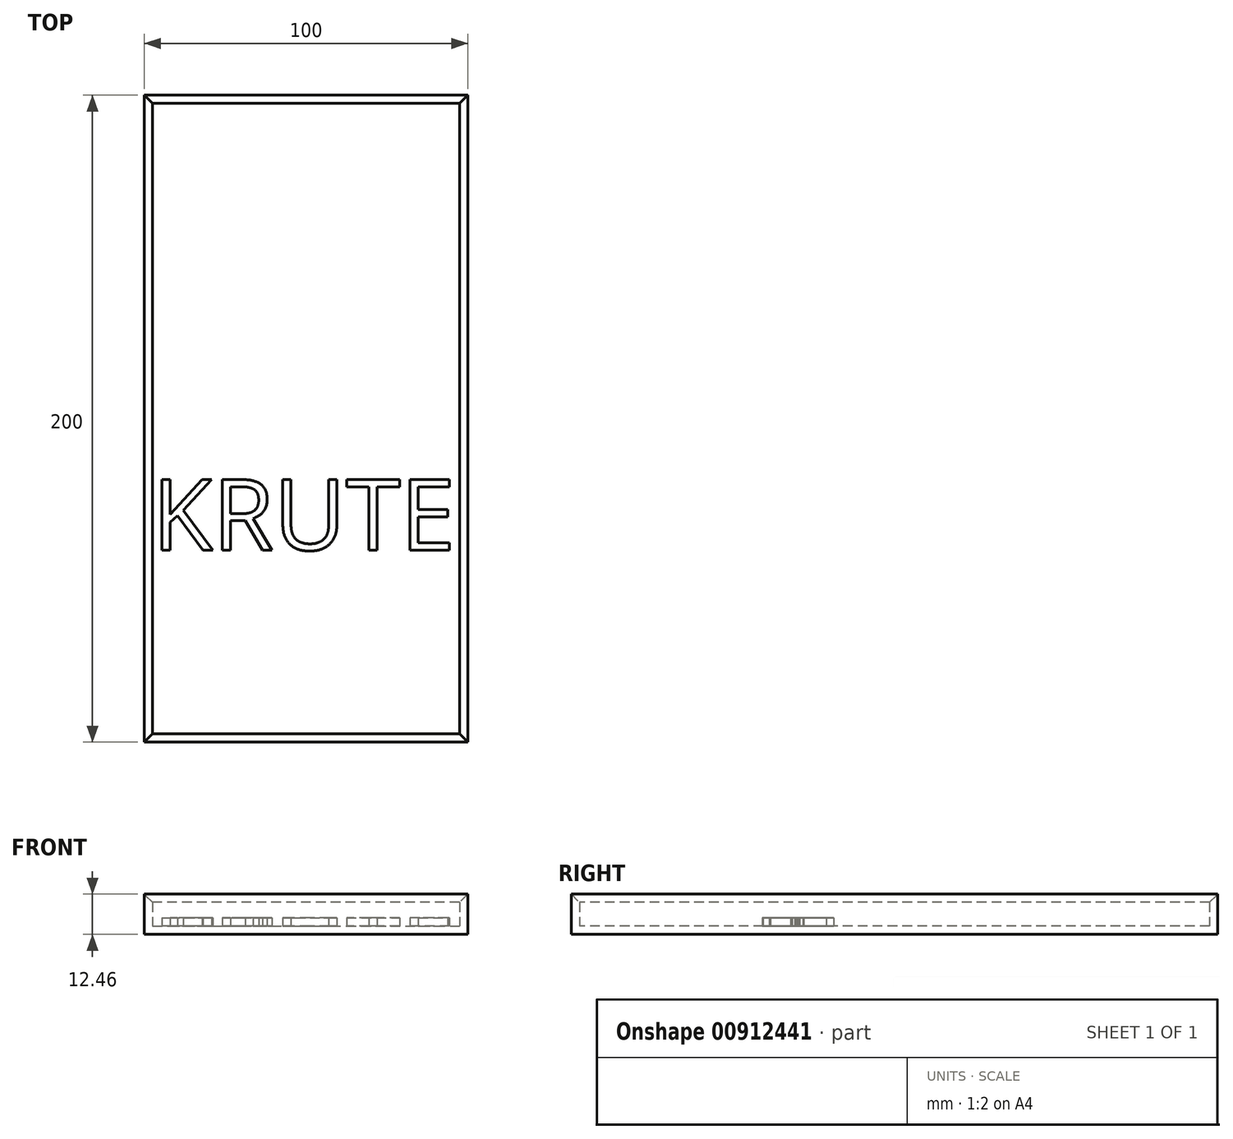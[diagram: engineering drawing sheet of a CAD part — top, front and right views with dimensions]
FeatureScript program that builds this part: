
annotation { "Feature Type Name" : "Feature", "Feature Type Description" : "" }
export const myFeature = defineFeature(function(context is Context, id is Id, definition is map)
    precondition{}
    {
        {
            var Q0;
            Q0=qCreatedBy(makeId("Top.planeOp"),FACE);
            var sketch = newSketch(context, id + "F0", { "sketchPlane" : qUnion([Q0])});
            skLineSegment(sketch, "E0.bottom", {"start": v(-49.36, 118.64) * mm, "end": v(50.64, 118.64) * mm});
            skLineSegment(sketch, "E0.top", {"start": v(-49.36, -81.36) * mm, "end": v(50.64, -81.36) * mm});
            skLineSegment(sketch, "E0.left", {"start": v(-49.36, 118.64) * mm, "end": v(-49.36, -81.36) * mm});
            skLineSegment(sketch, "E0.right", {"start": v(50.64, 118.64) * mm, "end": v(50.64, -81.36) * mm});
            skSolve(sketch);
        }
        {
            var Q0;
            Q0 = qSketchRegion(id + "F0", true);
            extrude(context, id + "F1", {"entities" : qUnion([Q0]), "depth" : 15 * mm, "offsetDistance" : 25.4 * mm});
        }
        {
            var Q0;
            Q0=makeQuery(id+"F1.opExtrude","CAP_FACE",FACE,{"disambiguationData":[OSD([sQuery(id+"F0.wireOp",EDGE,"E0.bottom"),sQuery(id+"F0.wireOp",EDGE,"E0.top"),sQuery(id+"F0.wireOp",EDGE,"E0.left"),sQuery(id+"F0.wireOp",EDGE,"E0.right")])],"isStart":false});
            shell(context, id + "F2", {"entities" : qUnion([Q0]), "thickness" : 2.54 * mm});
        }
        {
            var Q0;
            Q0=makeQuery(id+"F2.opShell","OFFSET_FACE",FACE,{"disambiguationData":[OSD([sQuery(id+"F0.wireOp",EDGE,"E0.bottom"),sQuery(id+"F0.wireOp",EDGE,"E0.top"),sQuery(id+"F0.wireOp",EDGE,"E0.left"),sQuery(id+"F0.wireOp",EDGE,"E0.right")])]});
            var sketch = newSketch(context, id + "F3", { "sketchPlane" : qUnion([Q0])});
            skText(sketch, "E1", { "text": "KRUTE", "fontName": "OpenSans-Regular.ttf"});
            const initialGuessF3  = {"E1": [-0.04694, -0.022, 1, 0, 0.022]};
            skSetInitialGuess(sketch, initialGuessF3);
            skSolve(sketch);
        }
        {
            var Q0;
            Q0 = qSketchRegion(id + "F3", true);
            extrude(context, id + "F4", {"entities" : qUnion([Q0]), "operationType" : NewBodyOperationType.ADD, "depth" : 2.54 * mm, "offsetDistance" : 25.4 * mm});
        }
        {
            var Q0;
            {var subQ0=sQuery(id+"F0.wireOp",EDGE,"E0.left");Q0=makeQuery(id+"F2.opShell","OFFSET_EDGE",EDGE,{"disambiguationData":[OSD([subQ0]),TDD([makeQuery(id+"F1.opExtrude","CAP_EDGE",EDGE,{"disambiguationData":[OSD([subQ0])],"isStart":false})])]});}
            var Q1;
            {var subQ0=sQuery(id+"F0.wireOp",EDGE,"E0.top");Q1=makeQuery(id+"F2.opShell","OFFSET_EDGE",EDGE,{"disambiguationData":[OSD([subQ0]),TDD([makeQuery(id+"F1.opExtrude","CAP_EDGE",EDGE,{"disambiguationData":[OSD([subQ0])],"isStart":false})])]});}
            var Q2;
            {var subQ0=sQuery(id+"F0.wireOp",EDGE,"E0.right");Q2=makeQuery(id+"F2.opShell","OFFSET_EDGE",EDGE,{"disambiguationData":[OSD([subQ0]),TDD([makeQuery(id+"F1.opExtrude","CAP_EDGE",EDGE,{"disambiguationData":[OSD([subQ0])],"isStart":false})])]});}
            var Q3;
            {var subQ0=sQuery(id+"F0.wireOp",EDGE,"E0.bottom");Q3=makeQuery(id+"F2.opShell","OFFSET_EDGE",EDGE,{"disambiguationData":[OSD([subQ0]),TDD([makeQuery(id+"F1.opExtrude","CAP_EDGE",EDGE,{"disambiguationData":[OSD([subQ0])],"isStart":false})])]});}
            chamfer(context, id + "F5", {"entities" : qUnion([Q0, Q1, Q2, Q3]), "width" : 5.08 * mm, "tangentPropagation" : true});
        }
    });
